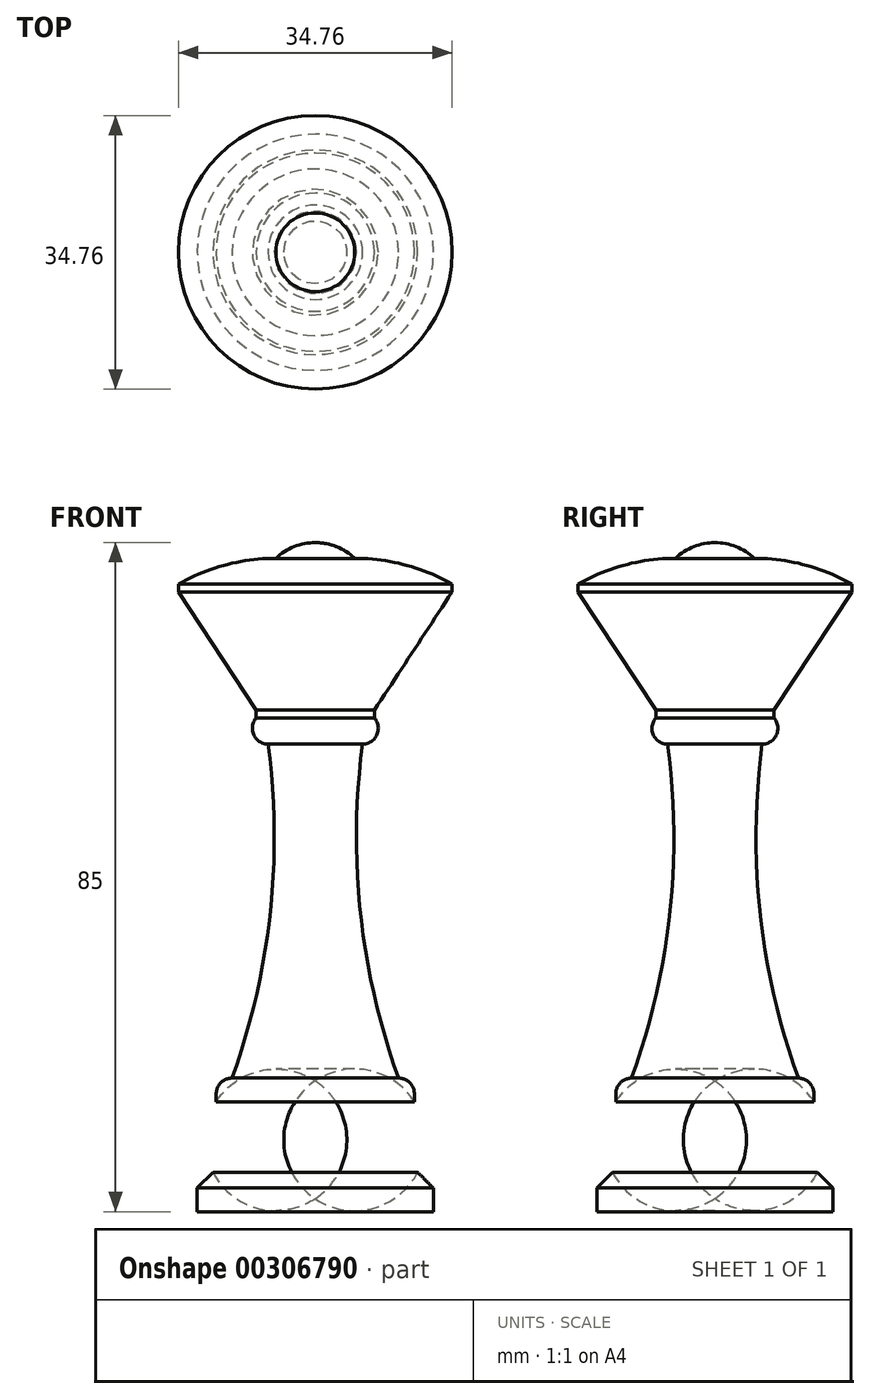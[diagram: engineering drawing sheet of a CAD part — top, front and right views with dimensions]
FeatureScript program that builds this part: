
annotation { "Feature Type Name" : "Feature", "Feature Type Description" : "" }
export const myFeature = defineFeature(function(context is Context, id is Id, definition is map)
    precondition{}
    {
        {
            var Q0;
            Q0=qCreatedBy(makeId("Front.planeOp"),FACE);
            var sketch = newSketch(context, id + "F0", { "sketchPlane" : qUnion([Q0])});
            skLineSegment(sketch, "E0", {"start": v(0, 0) * mm, "end": v(0, -85) * mm});
            skArc(sketch, "E1", {"start": v(5, -2) * mm, "mid": v(2.7, -0.52) * mm, "end": v(0, 0) * mm});
            skArc(sketch, "E2", {"start": v(17.38, -5.28) * mm, "mid": v(11.4, -2.83) * mm, "end": v(5, -2) * mm});
            skLineSegment(sketch, "E3", {"start": v(17.38, -5.28) * mm, "end": v(17.38, -6.28) * mm});
            skLineSegment(sketch, "E4", {"start": v(17.38, -6.28) * mm, "end": v(7.5, -21.28) * mm});
            skLineSegment(sketch, "E5", {"start": v(7.5, -21.28) * mm, "end": v(7.5, -22.28) * mm});
            skArc(sketch, "E6", {"start": v(6, -25.6) * mm, "mid": v(7.82, -24.42) * mm, "end": v(7.5, -22.28) * mm});
            skArc(sketch, "E7", {"start": v(6, -25.6) * mm, "mid": v(5.74, -47.1) * mm, "end": v(10.58, -68.03) * mm});
            skLineSegment(sketch, "E8", {"start": v(12.58, -70.03) * mm, "end": v(12.58, -71.03) * mm});
            skArc(sketch, "E9", {"start": v(13, -80) * mm, "mid": v(14, -75.46) * mm, "end": v(12.58, -71.03) * mm});
            skLineSegment(sketch, "E10", {"start": v(13, -80) * mm, "end": v(15, -82) * mm});
            skLineSegment(sketch, "E11", {"start": v(15, -82) * mm, "end": v(15, -85) * mm});
            skLineSegment(sketch, "E12", {"start": v(15, -85) * mm, "end": v(0, -85) * mm});
            skArc(sketch, "E13", {"start": v(12.58, -70.03) * mm, "mid": v(12, -68.62) * mm, "end": v(10.58, -68.03) * mm});
            skSolve(sketch);
        }
        {
            var Q0;
            Q0=makeQuery(id+"F0.imprint","IMPRINT",FACE,{"disambiguationData":[TD([[makeQuery(id+"F0.imprint","IMPRINT",EDGE,{"derivedFrom":sQuery(id+"F0.wireOp",EDGE,"E0")}),1.0]])]});
            var Q1;
            Q1=sQuery(id+"F0.wireOp",EDGE,"E0");
            revolve(context, id + "F1", {"entities" : qUnion([Q0]), "axis" : qUnion([Q1]), "revolveType" : RevolveType.FULL});
        }
    });
